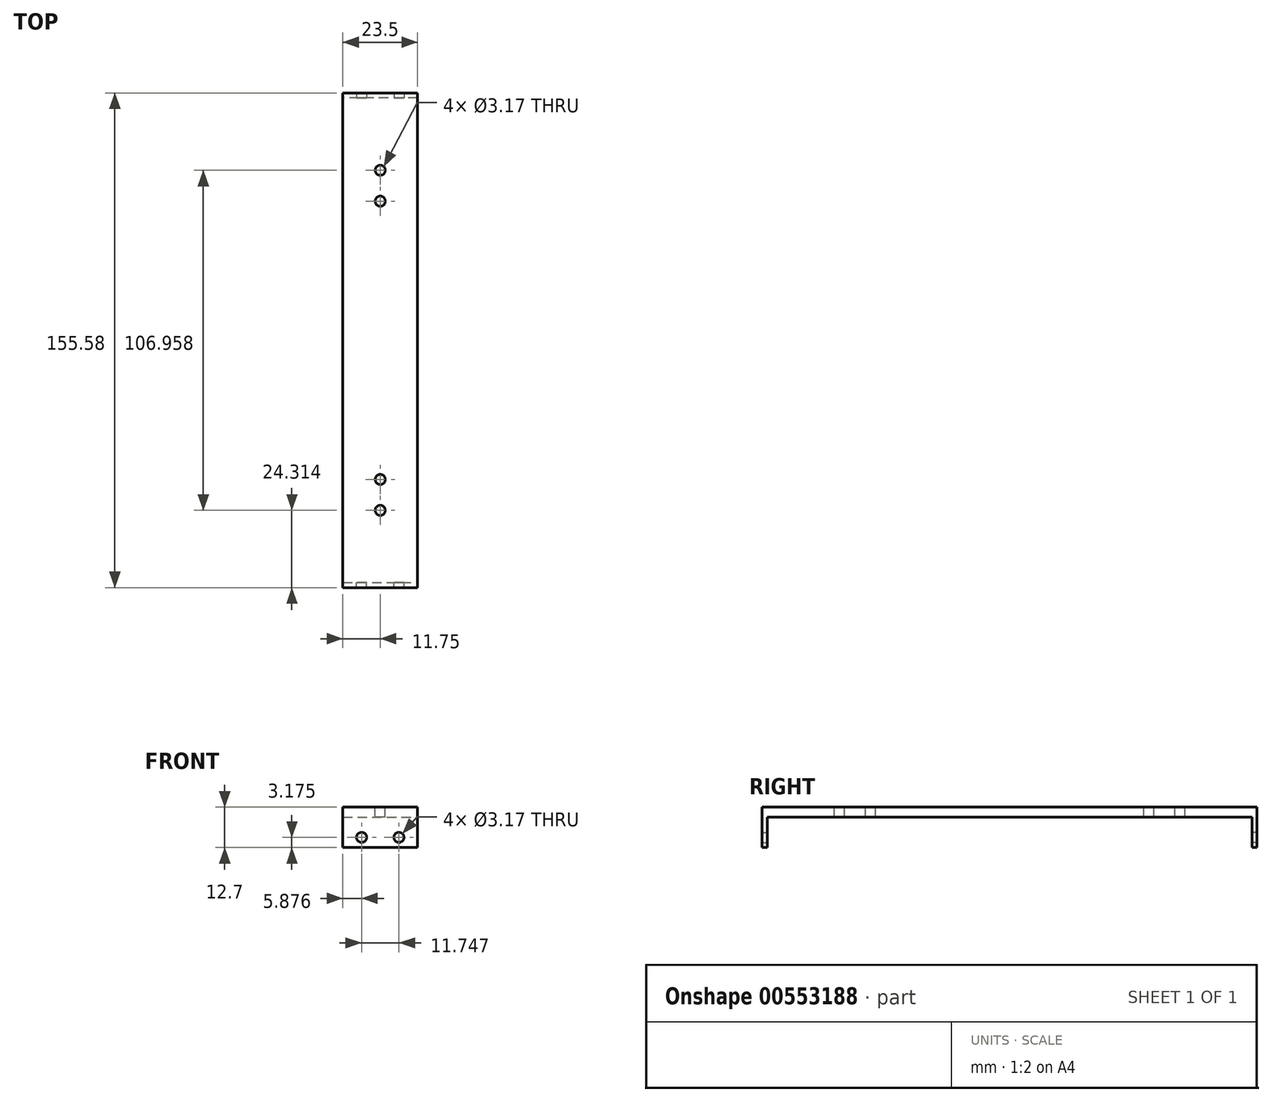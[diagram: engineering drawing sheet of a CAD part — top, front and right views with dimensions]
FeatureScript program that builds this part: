
annotation { "Feature Type Name" : "Feature", "Feature Type Description" : "" }
export const myFeature = defineFeature(function(context is Context, id is Id, definition is map)
    precondition{}
    {
        {
            var Q0;
            Q0=qCreatedBy(makeId("Front.planeOp"),FACE);
            var sketch = newSketch(context, id + "F0", { "sketchPlane" : qUnion([Q0])});
            skLineSegment(sketch, "E0.bottom", {"start": v(11.75, 6.35) * mm, "end": v(-11.75, 6.35) * mm});
            skLineSegment(sketch, "E0.top", {"start": v(11.75, -6.35) * mm, "end": v(-11.75, -6.35) * mm});
            skLineSegment(sketch, "E0.left", {"start": v(11.75, 6.35) * mm, "end": v(11.75, -6.35) * mm});
            skLineSegment(sketch, "E0.right", {"start": v(-11.75, 6.35) * mm, "end": v(-11.75, -6.35) * mm});
            skPoint(sketch, "E0.middle", {"position": v(0, 0) * mm});
            skSolve(sketch);
        }
        {
            var Q0;
            Q0=makeQuery(id+"F0.imprint","IMPRINT",FACE,{"disambiguationData":[TD([[makeQuery(id+"F0.imprint","IMPRINT",EDGE,{"derivedFrom":sQuery(id+"F0.wireOp",EDGE,"E0.bottom")}),1.0]])]});
            extrude(context, id + "F1", {"entities" : qUnion([Q0]), "depth" : 1.59 * mm, "offsetDistance" : 25.4 * mm});
        }
        {
            var Q0;
            Q0=makeQuery(id+"F1.opExtrude","CAP_FACE",FACE,{"disambiguationData":[OSD([sQuery(id+"F0.wireOp",EDGE,"E0.bottom"),sQuery(id+"F0.wireOp",EDGE,"E0.top"),sQuery(id+"F0.wireOp",EDGE,"E0.left"),sQuery(id+"F0.wireOp",EDGE,"E0.right")])],"isStart":false});
            var sketch = newSketch(context, id + "F2", { "sketchPlane" : qUnion([Q0])});
            skLineSegment(sketch, "E1", {"start": v(-11.75, 0) * mm, "end": v(0, 0) * mm, "construction": true});
            skLineSegment(sketch, "E2", {"start": v(0, 0) * mm, "end": v(11.75, 0) * mm, "construction": true});
            skLineSegment(sketch, "E3", {"start": v(-5.87, 0) * mm, "end": v(-5.87, -3.18) * mm, "construction": true});
            skLineSegment(sketch, "E4", {"start": v(5.87, 0) * mm, "end": v(5.87, -3.18) * mm, "construction": true});
            skCircle(sketch, "E5", {"center": v(-5.87, -3.18) * mm, "radius": 1.59 * mm});
            skCircle(sketch, "E6", {"center": v(5.87, -3.18) * mm, "radius": 1.59 * mm});
            skSolve(sketch);
        }
        {
            var Q0;
            Q0=makeQuery(id+"F2.imprint","IMPRINT",FACE,{"disambiguationData":[TD([[makeQuery(id+"F2.imprint","IMPRINT",EDGE,{"derivedFrom":sQuery(id+"F2.wireOp",EDGE,"E5")}),1.0]])]});
            var Q1;
            Q1=makeQuery(id+"F2.imprint","IMPRINT",FACE,{"disambiguationData":[TD([[makeQuery(id+"F2.imprint","IMPRINT",EDGE,{"derivedFrom":sQuery(id+"F2.wireOp",EDGE,"E6")}),1.0]])]});
            extrude(context, id + "F3", {"entities" : qUnion([Q0, Q1]), "operationType" : NewBodyOperationType.REMOVE, "oppositeDirection" : true, "depth" : 25.4 * mm, "offsetDistance" : 25.4 * mm});
        }
        {
            var Q0;
            Q0=makeQuery(id+"F1.opExtrude","CAP_FACE",FACE,{"disambiguationData":[OSD([sQuery(id+"F0.wireOp",EDGE,"E0.bottom"),sQuery(id+"F0.wireOp",EDGE,"E0.top"),sQuery(id+"F0.wireOp",EDGE,"E0.left"),sQuery(id+"F0.wireOp",EDGE,"E0.right")])],"isStart":false});
            var sketch = newSketch(context, id + "F4", { "sketchPlane" : qUnion([Q0])});
            skLineSegment(sketch, "E7.bottom", {"start": v(-11.75, 6.35) * mm, "end": v(11.75, 6.35) * mm});
            skLineSegment(sketch, "E7.top", {"start": v(-11.75, 3.17) * mm, "end": v(11.75, 3.17) * mm});
            skLineSegment(sketch, "E7.left", {"start": v(-11.75, 6.35) * mm, "end": v(-11.75, 3.17) * mm});
            skLineSegment(sketch, "E7.right", {"start": v(11.75, 6.35) * mm, "end": v(11.75, 3.17) * mm});
            skSolve(sketch);
        }
        {
            var Q0;
            Q0=makeQuery(id+"F4.imprint","IMPRINT",FACE,{"disambiguationData":[TD([[makeQuery(id+"F4.imprint","IMPRINT",EDGE,{"derivedFrom":sQuery(id+"F4.wireOp",EDGE,"E7.bottom")}),1.0]])]});
            extrude(context, id + "F5", {"entities" : qUnion([Q0]), "operationType" : NewBodyOperationType.ADD, "depth" : 76.2 * mm, "offsetDistance" : 25.4 * mm});
        }
        {
            var Q0;
            Q0=makeQuery(id+"F1.opExtrude","SWEPT_BODY",BODY,{"disambiguationData":[OSD([sQuery(id+"F0.wireOp",EDGE,"E0.bottom"),sQuery(id+"F0.wireOp",EDGE,"E0.top"),sQuery(id+"F0.wireOp",EDGE,"E0.left"),sQuery(id+"F0.wireOp",EDGE,"E0.right")])]});
            var Q1;
            Q1=makeQuery(id+"F5.opExtrude","CAP_FACE",FACE,{"disambiguationData":[OSD([sQuery(id+"F4.wireOp",EDGE,"E7.bottom"),sQuery(id+"F4.wireOp",EDGE,"E7.top"),sQuery(id+"F4.wireOp",EDGE,"E7.left"),sQuery(id+"F4.wireOp",EDGE,"E7.right")])],"isStart":false});
            mirror(context, id + "F6", {"operationType" : NewBodyOperationType.ADD, "entities" : qUnion([Q0]), "mirrorPlane" : qUnion([Q1])});
        }
        {
            var Q0;
            {var subQ0=makeQuery(id+"F5.boolean.opBoolean","MERGE",FACE,{"derivedFrom":[makeQuery(id+"F1.opExtrude","SWEPT_FACE",FACE,{"disambiguationData":[OSD([sQuery(id+"F0.wireOp",EDGE,"E0.bottom")])]}),makeQuery(id+"F5.opExtrude","SWEPT_FACE",FACE,{"disambiguationData":[OSD([sQuery(id+"F4.wireOp",EDGE,"E7.bottom")])]})]});Q0=makeQuery(id+"F6.boolean.opBoolean","MERGE",FACE,{"derivedFrom":[subQ0,makeQuery(id+"F6.opPattern","COPY",FACE,{"derivedFrom":subQ0,"instanceName":"1"})]});}
            var sketch = newSketch(context, id + "F7", { "sketchPlane" : qUnion([Q0])});
            skLineSegment(sketch, "E8", {"start": v(0, 0) * mm, "end": v(0, -77.79) * mm, "construction": true});
            skPoint(sketch, "E8.endSnap0", {"position": v(11.75, -77.79) * mm});
            skLineSegment(sketch, "E9", {"start": v(0, 0) * mm, "end": v(0, -38.9) * mm, "construction": true});
            skLineSegment(sketch, "E10", {"start": v(0, -38.9) * mm, "end": v(0, -19.45) * mm, "construction": true});
            skLineSegment(sketch, "E11", {"start": v(0, -29.17) * mm, "end": v(0, -38.9) * mm, "construction": true});
            skLineSegment(sketch, "E12", {"start": v(0, -29.17) * mm, "end": v(0, -19.45) * mm, "construction": true});
            skCircle(sketch, "E13", {"center": v(0, -34.03) * mm, "radius": 1.59 * mm});
            skCircle(sketch, "E14", {"center": v(0, -24.3) * mm, "radius": 1.59 * mm});
            skLineSegment(sketch, "E15", {"start": v(11.75, -77.79) * mm, "end": v(-11.75, -77.79) * mm, "construction": true});
            skCircle(sketch, "E16.MirrorC", {"center": v(0, -131.27) * mm, "radius": 1.59 * mm});
            skCircle(sketch, "E17.MirrorC", {"center": v(0, -121.54) * mm, "radius": 1.59 * mm});
            skSolve(sketch);
        }
        {
            var Q0;
            Q0 = qSketchRegion(id + "F7", true);
            extrude(context, id + "F8", {"entities" : qUnion([Q0]), "operationType" : NewBodyOperationType.REMOVE, "oppositeDirection" : true, "depth" : 25.4 * mm, "offsetDistance" : 25.4 * mm});
        }
    });
